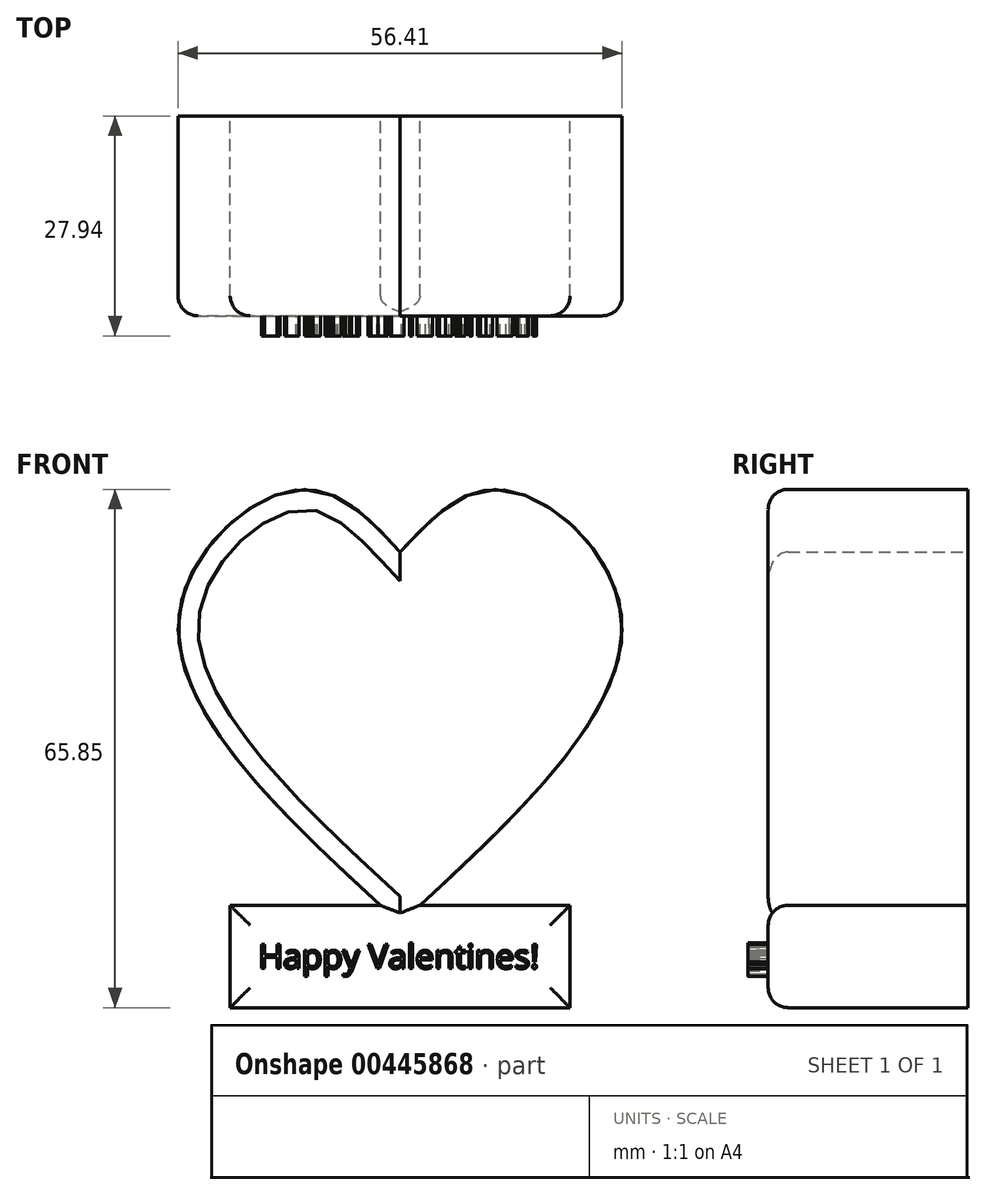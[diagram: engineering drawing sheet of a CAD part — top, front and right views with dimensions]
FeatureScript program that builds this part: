
annotation { "Feature Type Name" : "Feature", "Feature Type Description" : "" }
export const myFeature = defineFeature(function(context is Context, id is Id, definition is map)
    precondition{}
    {
        {
            var Q0;
            Q0=qCreatedBy(makeId("Front.planeOp"),FACE);
            var sketch = newSketch(context, id + "F0", { "sketchPlane" : qUnion([Q0])});
            skFitSpline(sketch, "E0", {"points": [v(-4.54, 17.44) * mm, v(-17.56, 25.35) * mm, v(-32.68, 9.07) * mm, v(-4.54, -29.77) * mm], "startDerivative": vector(-46.86, 50.28) * mm, "endDerivative": vector(98.58, -90.38) * mm});
            skFitSpline(sketch, "E1.MirrorCS", {"points": [v(-4.54, 17.44) * mm, v(8.49, 25.35) * mm, v(23.6, 9.07) * mm, v(-4.54, -29.77) * mm], "startDerivative": vector(46.86, 50.28) * mm, "endDerivative": vector(-98.58, -90.38) * mm});
            skSolve(sketch);
        }
        {
            var Q0;
            Q0=makeQuery(id+"F0.imprint","IMPRINT",FACE,{"disambiguationData":[TD([[makeQuery(id+"F0.imprint","IMPRINT",EDGE,{"derivedFrom":sQuery(id+"F0.wireOp",EDGE,"E0")}),1.0]])]});
            extrude(context, id + "F1", {"entities" : qUnion([Q0]), "depth" : 25.4 * mm});
        }
        {
            var Q0;
            Q0=qCreatedBy(makeId("Front.planeOp"),FACE);
            var sketch = newSketch(context, id + "F2", { "sketchPlane" : qUnion([Q0])});
            skLineSegment(sketch, "E2.bottom", {"start": v(-26.13, -27.46) * mm, "end": v(17.05, -27.46) * mm});
            skLineSegment(sketch, "E2.top", {"start": v(-26.13, -40.46) * mm, "end": v(17.05, -40.46) * mm});
            skLineSegment(sketch, "E2.left", {"start": v(-26.13, -27.46) * mm, "end": v(-26.13, -40.46) * mm});
            skLineSegment(sketch, "E2.right", {"start": v(17.05, -27.46) * mm, "end": v(17.05, -40.46) * mm});
            skSolve(sketch);
        }
        {
            var Q0;
            Q0 = qSketchRegion(id + "F2", true);
            extrude(context, id + "F3", {"entities" : qUnion([Q0]), "operationType" : NewBodyOperationType.ADD, "depth" : 25.4 * mm});
        }
        {
            var Q0;
            Q0=makeQuery(id+"F3.boolean.opBoolean","MERGE",FACE,{"derivedFrom":[makeQuery(id+"F1.opExtrude","CAP_FACE",FACE,{"disambiguationData":[OSD([sQuery(id+"F0.wireOp",EDGE,"E0"),sQuery(id+"F0.wireOp",EDGE,"E1.MirrorCS")])],"isStart":false}),makeQuery(id+"F3.opExtrude","CAP_FACE",FACE,{"disambiguationData":[OSD([sQuery(id+"F2.wireOp",EDGE,"E2.bottom"),sQuery(id+"F2.wireOp",EDGE,"E2.top"),sQuery(id+"F2.wireOp",EDGE,"E2.left"),sQuery(id+"F2.wireOp",EDGE,"E2.right")])],"isStart":false})]});
            fillet(context, id + "F4", {"entities" : qUnion([Q0]), "radius" : 2.54 * mm, "tangentPropagation" : true, "allowEdgeOverflow" : false});
        }
        {
            var Q0;
            Q0=qCreatedBy(makeId("Front.planeOp"),FACE);
            var sketch = newSketch(context, id + "F5", { "sketchPlane" : qUnion([Q0])});
            skText(sketch, "E3", { "text": "Happy Valentines! ", "fontName": "OpenSans-Regular.ttf"});
            const initialGuessF5  = {"E3": [-0.02254, -0.03548, 1, 0, 0.00306]};
            skSetInitialGuess(sketch, initialGuessF5);
            skSolve(sketch);
        }
        {
            var Q0;
            Q0 = qSketchRegion(id + "F5", true);
            extrude(context, id + "F6", {"entities" : qUnion([Q0]), "operationType" : NewBodyOperationType.ADD, "depth" : 27.94 * mm});
        }
    });
